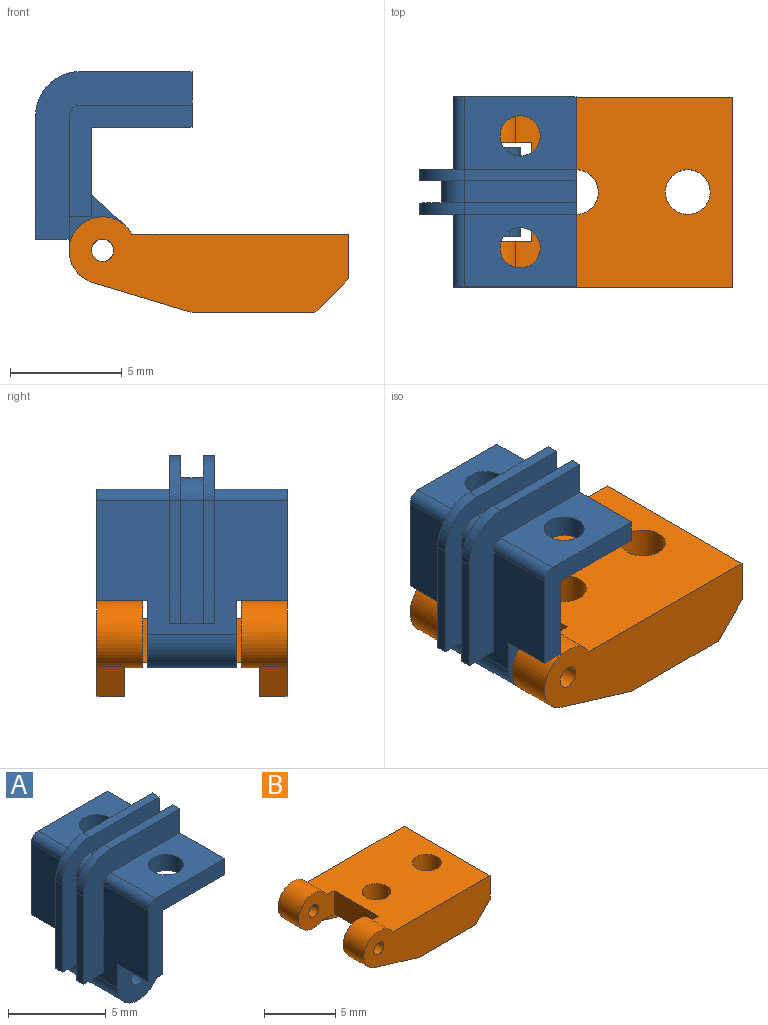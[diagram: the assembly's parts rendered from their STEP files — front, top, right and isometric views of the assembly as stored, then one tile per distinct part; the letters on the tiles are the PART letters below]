
ASSEMBLY  parts=2 mates=1
PART A: 33 faces, bbox 7x8.5x9.5 mm
  f0: plane 8.5x4.5mm, normal (0,0,-1), area 33.2mm2, adj f3,f6,f14,f17,f31,f32
  f1: plane 5x0.5mm, normal (0,0,1), area 2.5mm2, adj f3,f20,f24,f27
  f2: plane 5.5x0.5mm, normal (-1,0,0), area 2.8mm2, adj f4,f20,f24,f27
  f3: plane 8.5x2.5mm, normal (1,0,0), area 10.5mm2, adj f0,f1,f5,f10,f14,f17,f18,f20
  f4: plane 2x1.5mm, normal (0,0,-1), area 2mm2, adj f2,f9,f19,f20,f21,f23,f24,f25
  f5: plane 5x3.25mm, normal (0,0,1), area 13.7mm2, adj f3,f14,f21,f28,f32
  f6: plane 8.5x4mm, normal (1,0,0), area 30mm2, adj f0,f7,f12,f13,f14,f15,f16,f17
  f7: plane 4x1.52mm, normal (0.68,0,0.74), area 8.2mm2, adj f6,f8,f12,f13
  f8: cylinder r=1.5mm len=4mm, axis (0,-1,0), area 23.8mm2, adj f7,f9,f12,f13
  f9: plane 8.5x6mm, normal (-1,0,0), area 33.2mm2, adj f4,f8,f12,f13,f14,f15,f16,f17
  f10: plane 5x3.25mm, normal (0,0,1), area 13.7mm2, adj f3,f17,f20,f29,f31
  f11: cylinder r=0.5mm len=4mm, axis (0,-1,0), area 12.6mm2, adj f12,f13
  f12: plane 4x3mm, normal (0,1,0), area 7.3mm2, adj f6,f7,f8,f9,f11,f16
  f13: plane 4x3mm, normal (0,-1,0), area 7.3mm2, adj f6,f7,f8,f9,f11,f15
  f14: plane 5.5x5mm, normal (0,-1,0), area 9.4mm2, adj f0,f3,f5,f6,f9,f15,f28
  f15: plane 2.25x1mm, normal (0,0,-1), area 2.3mm2, adj f6,f9,f13,f14
  f16: plane 2.25x1mm, normal (0,0,-1), area 2.3mm2, adj f6,f9,f12,f17
  f17: plane 5.5x5mm, normal (0,1,0), area 9.4mm2, adj f0,f3,f6,f9,f10,f16,f29
  f18: plane 5x0.5mm, normal (0,0,1), area 2.5mm2, adj f3,f21,f25,f26
  f19: plane 5.5x0.5mm, normal (-1,0,0), area 2.8mm2, adj f4,f21,f25,f26
  f20: plane 7.5x7mm, normal (0,1,0), area 18.7mm2, adj f1,f2,f3,f4,f9,f10,f27,f29
  f21: plane 7.5x7mm, normal (0,-1,0), area 18.7mm2, adj f3,f4,f5,f9,f18,f19,f26,f28
  f22: plane 5x1mm, normal (0,0,1), area 5mm2, adj f3,f24,f25,f30
  f23: plane 5.5x1mm, normal (-1,0,0), area 5.5mm2, adj f4,f24,f25,f30
  f24: plane 7.5x7mm, normal (0,-1,0), area 12.9mm2, adj f1,f2,f3,f4,f22,f23,f27,f30
  f25: plane 7.5x7mm, normal (0,1,0), area 12.9mm2, adj f3,f4,f18,f19,f22,f23,f26,f30
  f26: cylinder r=2mm len=2mm, axis (0,1,0), area 1.6mm2, adj f18,f19,f21,f25
  f27: cylinder r=2mm len=2mm, axis (0,1,0), area 1.6mm2, adj f1,f2,f20,f24
  f28: cylinder r=0.5mm len=3.25mm, axis (0,1,0), area 2.6mm2, adj f5,f9,f14,f21
  f29: cylinder r=0.5mm len=3.25mm, axis (0,1,0), area 2.6mm2, adj f9,f10,f17,f20
  f30: cylinder r=1mm len=1mm, axis (0,1,0), area 1.6mm2, adj f22,f23,f24,f25
  f31: cylinder r=0.9mm len=1.8mm, axis (0,0,1), area 5.7mm2, adj f0,f10
  f32: cylinder r=0.9mm len=1.8mm, axis (0,0,1), area 5.7mm2, adj f0,f5
PART B: 22 faces, bbox 12.5x8.5x4.3 mm
  f0: plane 10.21x6mm, normal (0,0,-1), area 49.7mm2, adj f1,f2,f3,f7,f10,f12,f13,f14
  f1: cylinder r=1.5mm len=3mm, axis (0,1,0), area 13.1mm2, adj f0,f2,f4,f6,f8,f10
  f2: plane 3.5x3mm, normal (0,1,0), area 7.6mm2, adj f0,f1,f4,f5,f7
  f3: plane 8.5x2mm, normal (1,0,0), area 17mm2, adj f0,f4,f6,f11,f17,f21
  f4: plane 9.69x8.5mm, normal (0,0,1), area 73mm2, adj f1,f2,f3,f6,f7,f12,f13,f14
  f5: cylinder r=0.5mm len=2.05mm, axis (0,1,0), area 6.4mm2, adj f2,f6
  f6: plane 12.5x4.28mm, normal (0,-1,0), area 38.4mm2, adj f1,f3,f4,f5,f8,f9,f11
  f7: plane 4.4x2mm, normal (-1,0,0), area 8.8mm2, adj f0,f2,f4,f15
  f8: plane 4.43x1.34mm, normal (-0.29,0,-0.96), area 5.8mm2, adj f1,f6,f9,f10
  f9: plane 5.5x1.25mm, normal (0,0,-1), area 6.9mm2, adj f6,f8,f10,f11
  f10: plane 11.43x1.5mm, normal (0,1,0), area 12.8mm2, adj f0,f1,f8,f9,f11
  f11: plane 1.5x1.5mm, normal (0.71,0,-0.71), area 2.7mm2, adj f3,f6,f9,f10
  f12: cylinder r=1mm len=2mm, axis (0,0,-1), area 12.6mm2, adj f0,f4
  f13: cylinder r=1mm len=2mm, axis (0,0,-1), area 12.6mm2, adj f0,f4
  f14: cylinder r=1.5mm len=3mm, axis (0,-1,0), area 13.1mm2, adj f0,f4,f15,f17,f18,f20
  f15: plane 3.5x3mm, normal (0,-1,0), area 7.6mm2, adj f0,f4,f7,f14,f16
  f16: cylinder r=0.5mm len=2.05mm, axis (0,-1,0), area 6.4mm2, adj f15,f17
  f17: plane 12.5x4.28mm, normal (0,1,0), area 38.4mm2, adj f3,f4,f14,f16,f18,f19,f21
  f18: plane 4.43x1.34mm, normal (-0.29,0,-0.96), area 5.8mm2, adj f14,f17,f19,f20
  f19: plane 5.5x1.25mm, normal (0,0,-1), area 6.9mm2, adj f17,f18,f20,f21
  f20: plane 11.43x1.5mm, normal (0,-1,0), area 12.8mm2, adj f0,f14,f18,f19,f21
  f21: plane 1.5x1.5mm, normal (0.71,0,-0.71), area 2.7mm2, adj f3,f17,f19,f20
PLACE A t=(114.29,-100.86,-15.59)mm
PLACE B t=(114.29,-100.86,-15.59)mm
MATE cylindrical B.f1 <-> A.f8  axis (0,1,0) through (-235.64,-119.62,14.31)mm
